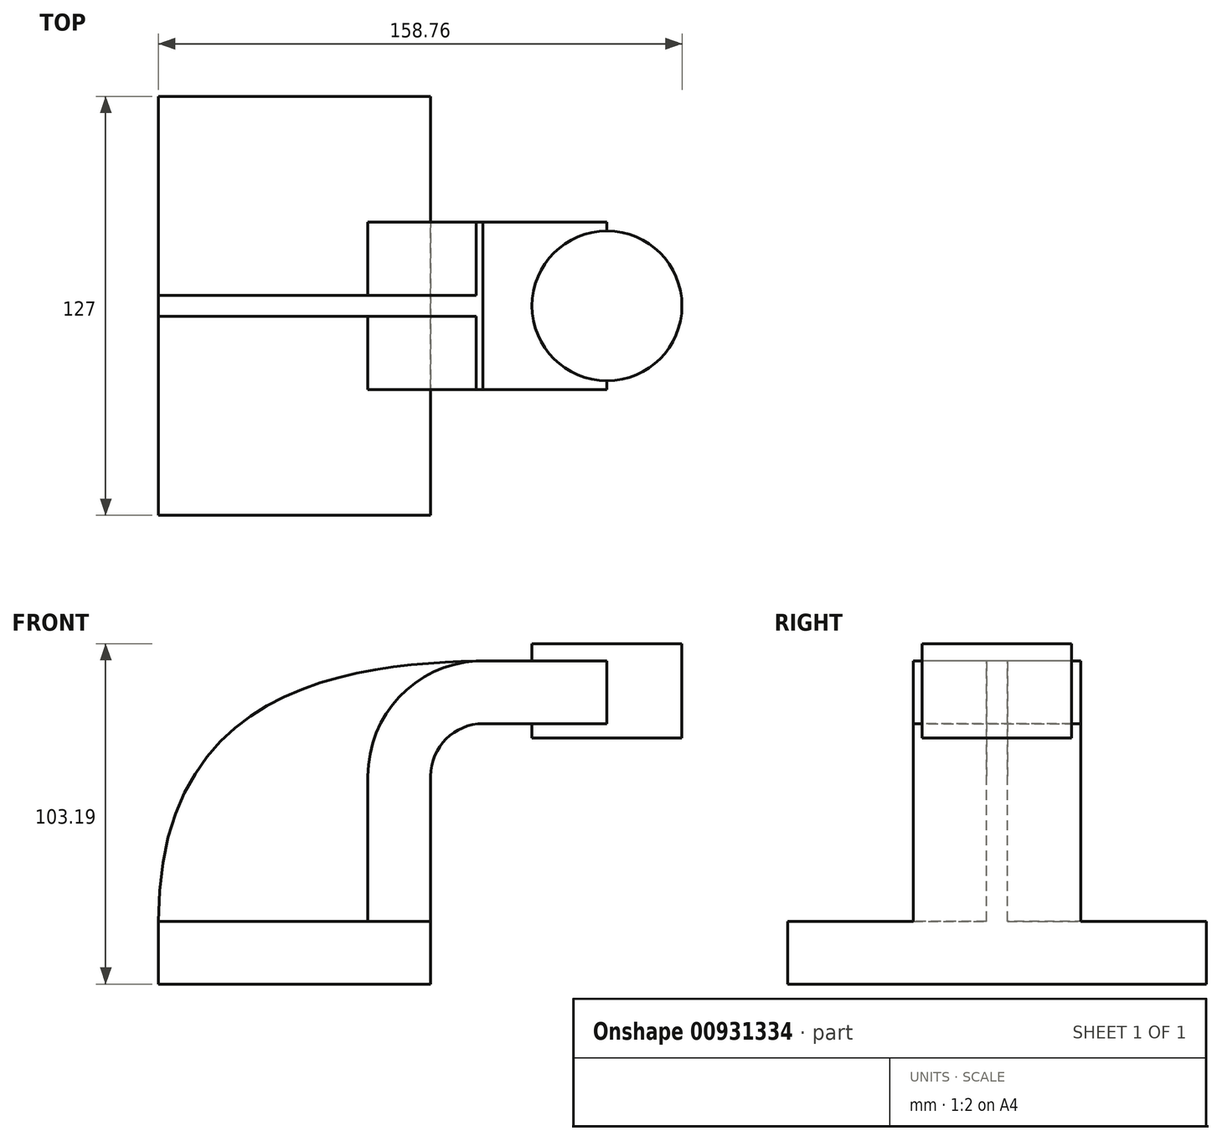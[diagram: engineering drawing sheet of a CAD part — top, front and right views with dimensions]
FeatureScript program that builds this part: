
annotation { "Feature Type Name" : "Feature", "Feature Type Description" : "" }
export const myFeature = defineFeature(function(context is Context, id is Id, definition is map)
    precondition{}
    {
        {
            var Q0;
            Q0=qCreatedBy(makeId("Front.planeOp"),FACE);
            var sketch = newSketch(context, id + "F0", { "sketchPlane" : qUnion([Q0])});
            skLineSegment(sketch, "E0.bottom", {"start": v(-41.27, -9.53) * mm, "end": v(41.28, -9.53) * mm});
            skLineSegment(sketch, "E0.top", {"start": v(-41.28, 9.52) * mm, "end": v(41.28, 9.52) * mm});
            skLineSegment(sketch, "E0.left", {"start": v(-41.28, -9.53) * mm, "end": v(-41.28, 9.52) * mm});
            skLineSegment(sketch, "E0.right", {"start": v(41.28, -9.53) * mm, "end": v(41.28, 9.52) * mm});
            skPoint(sketch, "E0.middle", {"position": v(0, 0) * mm});
            skLineSegment(sketch, "E1.bottom", {"start": v(66.67, 65.09) * mm, "end": v(117.47, 65.09) * mm});
            skLineSegment(sketch, "E1.top", {"start": v(66.67, 93.66) * mm, "end": v(117.47, 93.66) * mm});
            skLineSegment(sketch, "E1.left", {"start": v(66.67, 65.09) * mm, "end": v(66.67, 93.66) * mm});
            skLineSegment(sketch, "E1.right", {"start": v(117.47, 65.09) * mm, "end": v(117.47, 93.66) * mm});
            skPoint(sketch, "E1.middle", {"position": v(92.07, 79.38) * mm});
            skLineSegment(sketch, "E2", {"start": v(41.27, 9.52) * mm, "end": v(41.27, 53.57) * mm});
            skArc(sketch, "E3", {"start": v(41.28, 53.57) * mm, "mid": v(45.92, 64.8) * mm, "end": v(57.15, 69.45) * mm});
            skLineSegment(sketch, "E4", {"start": v(57.15, 69.45) * mm, "end": v(94.74, 69.45) * mm});
            skLineSegment(sketch, "E5.0", {"start": v(57.15, 88.5) * mm, "end": v(94.74, 88.5) * mm});
            skArc(sketch, "E5.1", {"start": v(22.23, 53.57) * mm, "mid": v(32.45, 78.27) * mm, "end": v(57.15, 88.5) * mm});
            skLineSegment(sketch, "E5.2", {"start": v(22.22, 9.52) * mm, "end": v(22.22, 53.57) * mm});
            skLineSegment(sketch, "E6", {"start": v(94.74, 65.09) * mm, "end": v(94.74, 93.66) * mm});
            skPoint(sketch, "E6.startSnap0", {"position": v(92.07, 65.09) * mm});
            skFitSpline(sketch, "E7", {"points": [v(-41.27, 9.52) * mm, v(57.15, 88.5) * mm], "startDerivative": vector(-0.85, 226.07) * mm, "endDerivative": vector(98.9, 2.9) * mm});
            skSolve(sketch);
        }
        {
            var Q0;
            Q0=makeQuery(id+"F0.imprint","IMPRINT",FACE,{"disambiguationData":[TD([[makeQuery(id+"F0.imprint","IMPRINT",EDGE,{"derivedFrom":sQuery(id+"F0.wireOp",EDGE,"E0.bottom")}),1.0]])]});
            extrude(context, id + "F1", {"entities" : qUnion([Q0]), "endBound" : BoundingType.SYMMETRIC, "oppositeDirection" : true, "depth" : 127 * mm, "offsetDistance" : 25.4 * mm});
        }
        {
            var Q0;
            {var subQ1=sQuery(id+"F0.wireOp",EDGE,"E2");Q0=makeQuery(id+"F0.imprint","IMPRINT",FACE,{"disambiguationData":[TD([[makeQuery(id+"F0.imprint","IMPRINT",EDGE,{"derivedFrom":subQ1}),1.0]])]});}
            var Q1;
            {var subQ0=sQuery(id+"F0.wireOp",EDGE,"E4");var subQ1=sQuery(id+"F0.wireOp",EDGE,"E1.left");var subQ2=makeQuery(id+"F0.imprint","INTERSECT",VERTEX,{"derivedFrom":[subQ1,subQ0]});Q1=makeQuery(id+"F0.imprint","IMPRINT",FACE,{"disambiguationData":[TD([[makeQuery(id+"F0.imprint","IMPRINT",EDGE,{"disambiguationData":[TD([[subQ2,-1.0]])],"derivedFrom":subQ1}),-1.0]])]});}
            extrude(context, id + "F2", {"entities" : qUnion([Q0, Q1]), "operationType" : NewBodyOperationType.ADD, "endBound" : BoundingType.SYMMETRIC, "depth" : 50.8 * mm, "offsetDistance" : 25.4 * mm});
        }
        {
            var Q0;
            {var subQ3=sQuery(id+"F0.wireOp",EDGE,"E5.2");Q0=makeQuery(id+"F0.imprint","IMPRINT",FACE,{"disambiguationData":[TD([[makeQuery(id+"F0.imprint","IMPRINT",EDGE,{"derivedFrom":subQ3}),1.0]])]});}
            extrude(context, id + "F3", {"entities" : qUnion([Q0]), "operationType" : NewBodyOperationType.ADD, "endBound" : BoundingType.SYMMETRIC, "depth" : 6.35 * mm, "offsetDistance" : 25.4 * mm});
        }
        {
            var Q0;
            {var subQ4=sQuery(id+"F0.wireOp",EDGE,"E1.right");Q0=makeQuery(id+"F0.imprint","IMPRINT",FACE,{"disambiguationData":[TD([[makeQuery(id+"F0.imprint","IMPRINT",EDGE,{"derivedFrom":subQ4}),1.0]])]});}
            var Q1;
            Q1=sQuery(id+"F0.wireOp",EDGE,"E6");
            revolve(context, id + "F4", {"operationType" : NewBodyOperationType.ADD, "surfaceOperationType" : NewSurfaceOperationType.NEW, "entities" : qUnion([Q0]), "axis" : qUnion([Q1]), "revolveType" : RevolveType.FULL});
        }
    });
